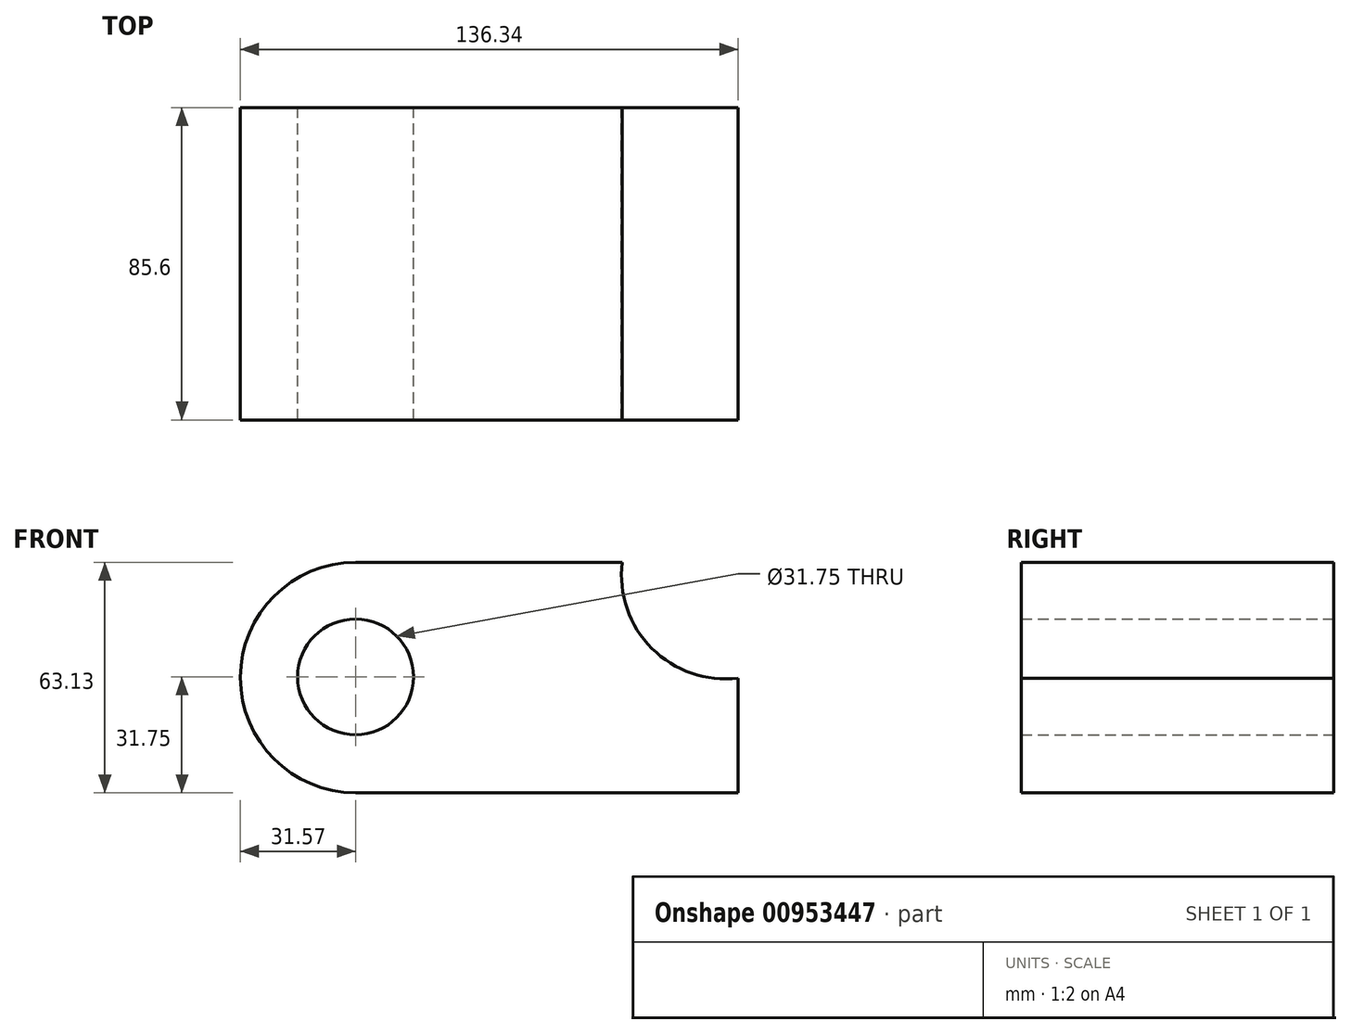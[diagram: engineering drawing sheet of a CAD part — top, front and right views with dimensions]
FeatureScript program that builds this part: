
annotation { "Feature Type Name" : "Feature", "Feature Type Description" : "" }
export const myFeature = defineFeature(function(context is Context, id is Id, definition is map)
    precondition{}
    {
        {
            var Q0;
            Q0=qCreatedBy(makeId("Front.planeOp"),FACE);
            var sketch = newSketch(context, id + "F0", { "sketchPlane" : qUnion([Q0])});
            skLineSegment(sketch, "E0", {"start": v(0, 0) * mm, "end": v(104.78, 0) * mm});
            skCircle(sketch, "E1", {"center": v(0, 31.75) * mm, "radius": 15.88 * mm});
            skArc(sketch, "E2", {"start": v(73.03, 63.13) * mm, "mid": v(81.2, 39.55) * mm, "end": v(104.78, 31.38) * mm});
            skLineSegment(sketch, "E3", {"start": v(0, 63.13) * mm, "end": v(73.03, 63.13) * mm});
            skLineSegment(sketch, "E4", {"start": v(104.78, 31.38) * mm, "end": v(104.78, 0) * mm});
            skArc(sketch, "E5", {"start": v(0, 63.13) * mm, "mid": v(-31.57, 31.57) * mm, "end": v(0, 0) * mm});
            skSolve(sketch);
        }
        {
            var Q0;
            Q0 = qSketchRegion(id + "F0", true);
            extrude(context, id + "F1", {"entities" : qUnion([Q0]), "depth" : 85.6 * mm, "offsetDistance" : 25.4 * mm});
        }
    });
